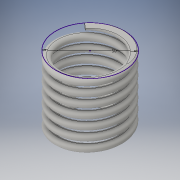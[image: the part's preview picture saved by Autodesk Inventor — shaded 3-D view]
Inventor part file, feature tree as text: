
AUTODESK INVENTOR PART (.ipt)
format: ipt  version: 2016 (Build 200138000, 138)  size: 374,272 bytes
history: native  units: in
note: dims shown in document units (in); Inventor stores cm internally (conversion verified against a paired STEP export)
features: sketch x3, extrude x1, helix x1, projected_geometry x1
ambient origin geometry x8: Origin, YZ Plane, XZ Plane, XY Plane, X Axis, Y Axis, Z Axis, Center Point
bodies: Body1 (feature_tree)
feature tree (6):
  extrude  "Extrusion5"  Depth=19.685in TaperAngle=0.0deg
  helix  "Coil3"  [1 undecoded]
  sketch  "Sketch15"  dims[d40=19.685in]
  sketch  "Sketch13"  dims[d28=19.685in d29=19.685in d30=0.0in d31=1.9685in]
  sketch  "Sketch14"  dims[d32=2.7559in d33=19.685in d34=0.3937in d35=0.0in d36=90.0deg d37=90.0deg d38=0.0in d39=0.0in]
  projected_geometry  "Project Cut Edges3"
note: 1 required parameter value undecoded (feature->parameter linkage not recoverable at this tier; creation-order binding heuristic only, values carry confidence <= 0.55)
